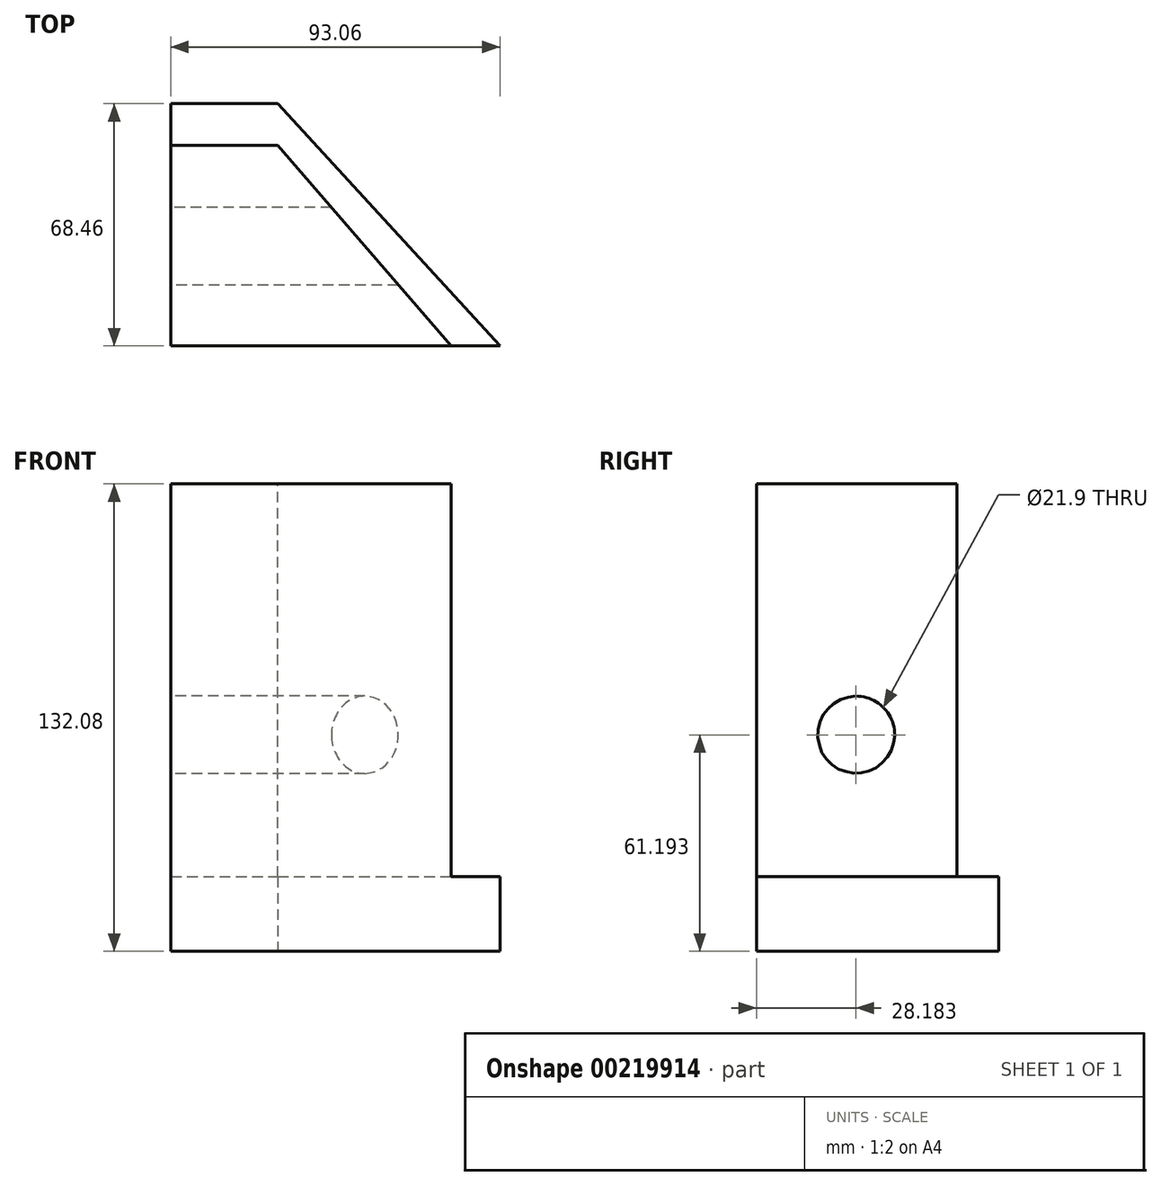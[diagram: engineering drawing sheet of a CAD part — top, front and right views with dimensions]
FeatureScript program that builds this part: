
annotation { "Feature Type Name" : "Feature", "Feature Type Description" : "" }
export const myFeature = defineFeature(function(context is Context, id is Id, definition is map)
    precondition{}
    {
        {
            var Q0;
            Q0=qCreatedBy(makeId("Top.planeOp"),FACE);
            var sketch = newSketch(context, id + "F0", { "sketchPlane" : qUnion([Q0])});
            skLineSegment(sketch, "E0", {"start": v(-24.25, 0) * mm, "end": v(-24.25, 68.46) * mm});
            skLineSegment(sketch, "E1", {"start": v(-24.25, 68.46) * mm, "end": v(6, 68.46) * mm});
            skLineSegment(sketch, "E2", {"start": v(6, 68.46) * mm, "end": v(68.81, 0) * mm});
            skLineSegment(sketch, "E3", {"start": v(68.81, 0) * mm, "end": v(-24.25, 0) * mm});
            skSolve(sketch);
        }
        {
            var Q0;
            Q0 = qSketchRegion(id + "F0", true);
            extrude(context, id + "F1", {"entities" : qUnion([Q0]), "depth" : 132.08 * mm});
        }
        {
            var Q0;
            Q0=makeQuery(id+"F1.opExtrude","CAP_FACE",FACE,{"disambiguationData":[OSD([sQuery(id+"F0.wireOp",EDGE,"E0"),sQuery(id+"F0.wireOp",EDGE,"E1"),sQuery(id+"F0.wireOp",EDGE,"E2"),sQuery(id+"F0.wireOp",EDGE,"E3")])],"isStart":false});
            var sketch = newSketch(context, id + "F2", { "sketchPlane" : qUnion([Q0])});
            skLineSegment(sketch, "E4", {"start": v(-24.25, 56.69) * mm, "end": v(6, 56.69) * mm});
            skLineSegment(sketch, "E5", {"start": v(6, 56.69) * mm, "end": v(54.96, 0) * mm});
            skLineSegment(sketch, "E6", {"start": v(54.96, 0) * mm, "end": v(68.81, 0) * mm});
            skLineSegment(sketch, "E7", {"start": v(68.81, 0) * mm, "end": v(6, 68.46) * mm});
            skLineSegment(sketch, "E8", {"start": v(6, 68.46) * mm, "end": v(-24.25, 68.46) * mm});
            skLineSegment(sketch, "E9", {"start": v(-24.25, 68.46) * mm, "end": v(-24.25, 56.69) * mm});
            skSolve(sketch);
        }
        {
            var Q0;
            Q0 = qSketchRegion(id + "F2", true);
            extrude(context, id + "F3", {"entities" : qUnion([Q0]), "operationType" : NewBodyOperationType.REMOVE, "oppositeDirection" : true, "depth" : 111 * mm});
        }
        {
            var Q0;
            Q0=makeQuery(id+"F1.opExtrude","SWEPT_FACE",FACE,{"disambiguationData":[OSD([sQuery(id+"F0.wireOp",EDGE,"E0")])]});
            var sketch = newSketch(context, id + "F4", { "sketchPlane" : qUnion([Q0])});
            skCircle(sketch, "E10", {"center": v(-28.18, 61.2) * mm, "radius": 10.95 * mm});
            skSolve(sketch);
        }
        {
            var Q0;
            Q0 = qSketchRegion(id + "F4", true);
            extrude(context, id + "F5", {"entities" : qUnion([Q0]), "operationType" : NewBodyOperationType.REMOVE, "oppositeDirection" : true, "depth" : 77.47 * mm});
        }
    });
